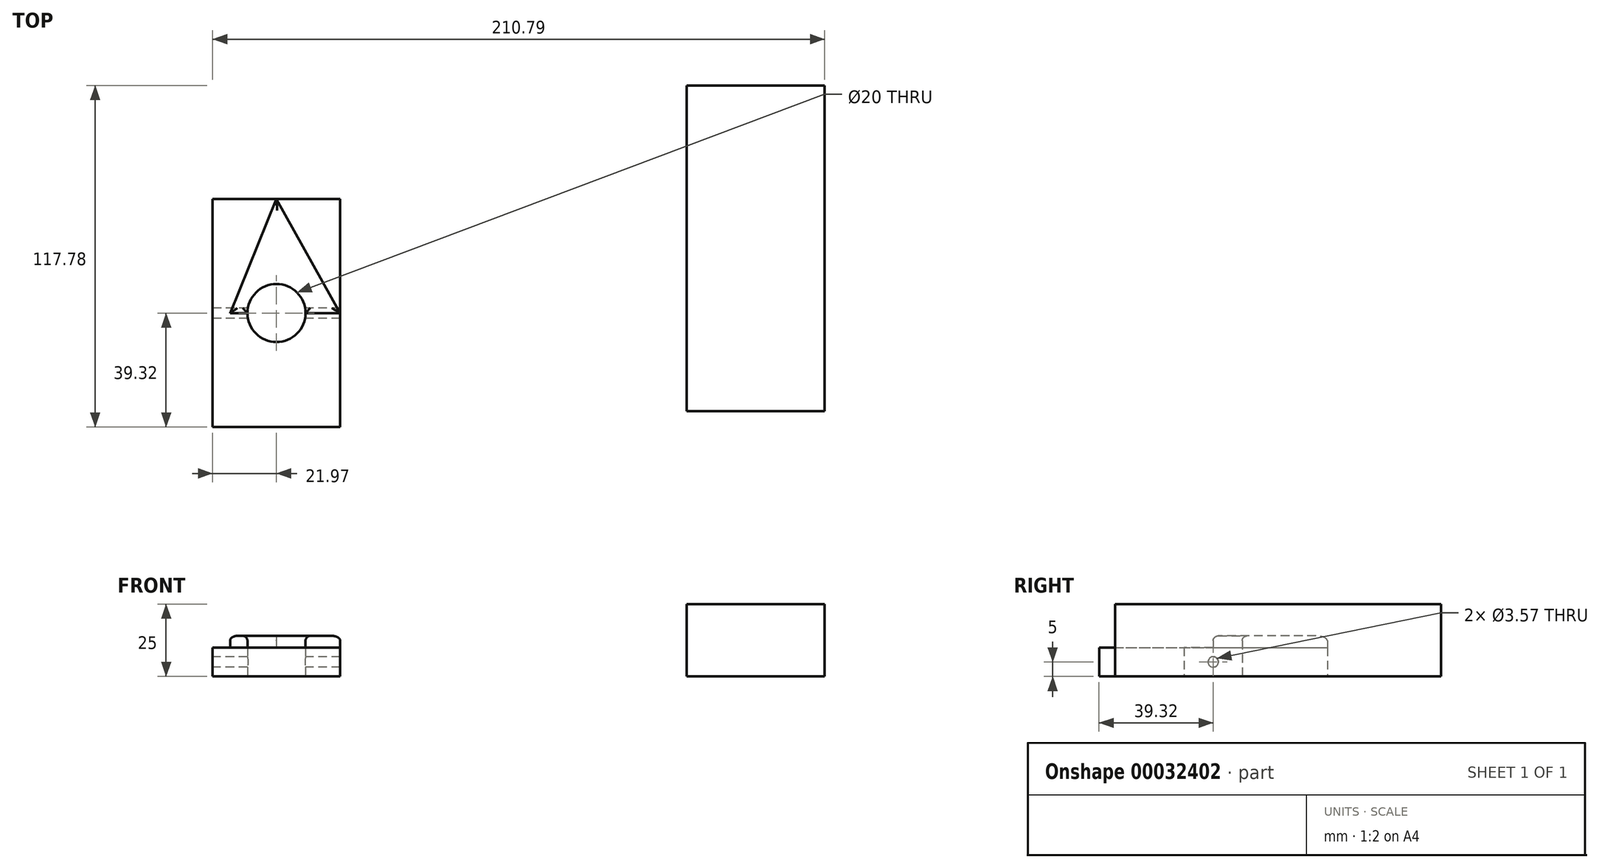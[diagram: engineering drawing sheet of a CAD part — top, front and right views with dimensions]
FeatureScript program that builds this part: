
annotation { "Feature Type Name" : "Feature", "Feature Type Description" : "" }
export const myFeature = defineFeature(function(context is Context, id is Id, definition is map)
    precondition{}
    {
        {
            var Q0;
            Q0=qCreatedBy(makeId("Top.planeOp"),FACE);
            var sketch = newSketch(context, id + "F0", { "sketchPlane" : qUnion([Q0])});
            skCircle(sketch, "E0.cCircle", {"center": v(0, 0) * mm, "radius": 5.5 * mm, "construction": true});
            skLineSegment(sketch, "E0.0", {"start": v(0, 5.5) * mm, "end": v(4.76, 2.75) * mm});
            skLineSegment(sketch, "E0.1", {"start": v(4.76, 2.75) * mm, "end": v(4.76, -2.75) * mm});
            skLineSegment(sketch, "E0.2", {"start": v(4.76, -2.75) * mm, "end": v(0, -5.5) * mm});
            skLineSegment(sketch, "E0.3", {"start": v(0, -5.5) * mm, "end": v(-4.76, -2.75) * mm});
            skLineSegment(sketch, "E0.4", {"start": v(-4.76, -2.75) * mm, "end": v(-4.76, 2.75) * mm});
            skLineSegment(sketch, "E0.5", {"start": v(-4.76, 2.75) * mm, "end": v(0, 5.5) * mm});
            skCircle(sketch, "E1", {"center": v(0, 0) * mm, "radius": 10 * mm});
            skLineSegment(sketch, "E2.rect.bottom", {"start": v(21.97, -39.32) * mm, "end": v(-21.97, -39.32) * mm});
            skLineSegment(sketch, "E2.rect.top", {"start": v(21.97, 39.32) * mm, "end": v(-21.97, 39.32) * mm});
            skLineSegment(sketch, "E2.rect.left", {"start": v(21.97, -39.32) * mm, "end": v(21.97, 39.32) * mm});
            skLineSegment(sketch, "E2.rect.right", {"start": v(-21.97, -39.32) * mm, "end": v(-21.97, 39.32) * mm});
            skSolve(sketch);
        }
        {
            var Q0;
            Q0=makeQuery(id+"F0.imprint","IMPRINT",FACE,{"disambiguationData":[TD([[makeQuery(id+"F0.imprint","IMPRINT",EDGE,{"derivedFrom":sQuery(id+"F0.wireOp",EDGE,"E1")}),-1.0]])]});
            extrude(context, id + "F1", {"entities" : qUnion([Q0]), "depth" : 10 * mm});
        }
        {
            var Q0;
            Q0=makeQuery(id+"F1.opExtrude","SWEPT_FACE",FACE,{"disambiguationData":[OSD([sQuery(id+"F0.wireOp",EDGE,"E2.rect.right")])]});
            var sketch = newSketch(context, id + "F2", { "sketchPlane" : qUnion([Q0])});
            skCircle(sketch, "E3", {"center": v(0, 5) * mm, "radius": 1.79 * mm});
            skPoint(sketch, "E3.centerSnap0", {"position": v(-39.32, 5) * mm});
            skPoint(sketch, "E3.centerSnap1", {"position": v(0, 10) * mm});
            skSolve(sketch);
        }
        {
            var Q0;
            Q0=makeQuery(id+"F2.imprint","IMPRINT",FACE,{"disambiguationData":[TD([[makeQuery(id+"F2.imprint","IMPRINT",EDGE,{"derivedFrom":sQuery(id+"F2.wireOp",EDGE,"E3")}),1.0]])]});
            var Q1;
            Q1=makeQuery(id+"F1.opExtrude","SWEPT_FACE",FACE,{"disambiguationData":[OSD([sQuery(id+"F0.wireOp",EDGE,"E2.rect.left")])]});
            var Q2;
            Q2=makeQuery(id+"F1.opExtrude","SWEPT_FACE",FACE,{"disambiguationData":[OSD([sQuery(id+"F0.wireOp",EDGE,"E2.rect.left")])]});
            extrude(context, id + "F3", {"entities" : qUnion([Q0]), "operationType" : NewBodyOperationType.REMOVE, "endBound" : BoundingType.UP_TO_SURFACE, "oppositeDirection" : true, "endBoundEntityFace" : qUnion([Q1]), "depth" : 50.3 * mm});
        }
        {
            var Q0;
            Q0=makeQuery(id+"F1.opExtrude","CAP_FACE",FACE,{"disambiguationData":[OSD([sQuery(id+"F0.wireOp",EDGE,"E1"),sQuery(id+"F0.wireOp",EDGE,"E2.rect.bottom"),sQuery(id+"F0.wireOp",EDGE,"E2.rect.top"),sQuery(id+"F0.wireOp",EDGE,"E2.rect.left"),sQuery(id+"F0.wireOp",EDGE,"E2.rect.right")])],"isStart":false});
            var sketch = newSketch(context, id + "F4", { "sketchPlane" : qUnion([Q0])});
            skLineSegment(sketch, "E4", {"start": v(-21.97, 0) * mm, "end": v(-10, 0) * mm});
            skLineSegment(sketch, "E5", {"start": v(-15.98, 0) * mm, "end": v(0, 39.32) * mm});
            skLineSegment(sketch, "E6", {"start": v(0, 39.32) * mm, "end": v(21.97, 0) * mm});
            skLineSegment(sketch, "E7", {"start": v(21.97, 0) * mm, "end": v(10, 0) * mm});
            skSolve(sketch);
        }
        {
            var Q0;
            {var subQ1=sQuery(id+"F4.wireOp",EDGE,"E5");Q0=makeQuery(id+"F4.imprint","IMPRINT",FACE,{"disambiguationData":[TD([[makeQuery(id+"F4.imprint","IMPRINT",EDGE,{"derivedFrom":subQ1}),-1.0]])]});}
            extrude(context, id + "F5", {"entities" : qUnion([Q0]), "operationType" : NewBodyOperationType.ADD, "depth" : 4 * mm, "offsetDistance" : 25 * mm});
        }
        {
            var Q0;
            Q0=makeQuery(id+"F5.opExtrude","CAP_EDGE",EDGE,{"disambiguationData":[OSD([sQuery(id+"F4.wireOp",EDGE,"E6")])],"isStart":false});
            var Q1;
            Q1=makeQuery(id+"F5.opExtrude","CAP_EDGE",EDGE,{"disambiguationData":[OSD([sQuery(id+"F4.wireOp",EDGE,"E5")])],"isStart":false});
            var Q2;
            Q2=makeQuery(id+"F5.opExtrude","CAP_EDGE",EDGE,{"disambiguationData":[OSD([sQuery(id+"F0.wireOp",EDGE,"E1")])],"isStart":false});
            var Q3;
            Q3=makeQuery(id+"F5.opExtrude","CAP_EDGE",EDGE,{"disambiguationData":[OSD([sQuery(id+"F4.wireOp",EDGE,"E4")])],"isStart":false});
            var Q4;
            Q4=makeQuery(id+"F5.opExtrude","CAP_EDGE",EDGE,{"disambiguationData":[OSD([sQuery(id+"F4.wireOp",EDGE,"E7")])],"isStart":false});
            fillet(context, id + "F6", {"entities" : qUnion([Q0, Q1, Q2, Q3, Q4]), "tangentPropagation" : true, "radius" : 1.69 * mm, "defaultsChanged" : false, "vertexSettings" : [], "allowEdgeOverflow" : false});
        }
        {
            var Q0;
            Q0=qCreatedBy(makeId("Top.planeOp"),FACE);
            var sketch = newSketch(context, id + "F7", { "sketchPlane" : qUnion([Q0])});
            skLineSegment(sketch, "E8.bottom", {"start": v(188.82, 78.46) * mm, "end": v(141.24, 78.46) * mm});
            skLineSegment(sketch, "E8.top", {"start": v(188.82, -33.84) * mm, "end": v(141.24, -33.84) * mm});
            skLineSegment(sketch, "E8.left", {"start": v(188.82, 78.46) * mm, "end": v(188.82, -33.84) * mm});
            skLineSegment(sketch, "E8.right", {"start": v(141.24, 78.46) * mm, "end": v(141.24, -33.84) * mm});
            skSolve(sketch);
        }
        {
            var Q0;
            Q0=makeQuery(id+"F7.imprint","IMPRINT",FACE,{"disambiguationData":[TD([[makeQuery(id+"F7.imprint","IMPRINT",EDGE,{"derivedFrom":sQuery(id+"F7.wireOp",EDGE,"E8.bottom")}),1.0]])]});
            extrude(context, id + "F8", {"entities" : qUnion([Q0]), "depth" : 25 * mm, "offsetDistance" : 25 * mm});
        }
    });
